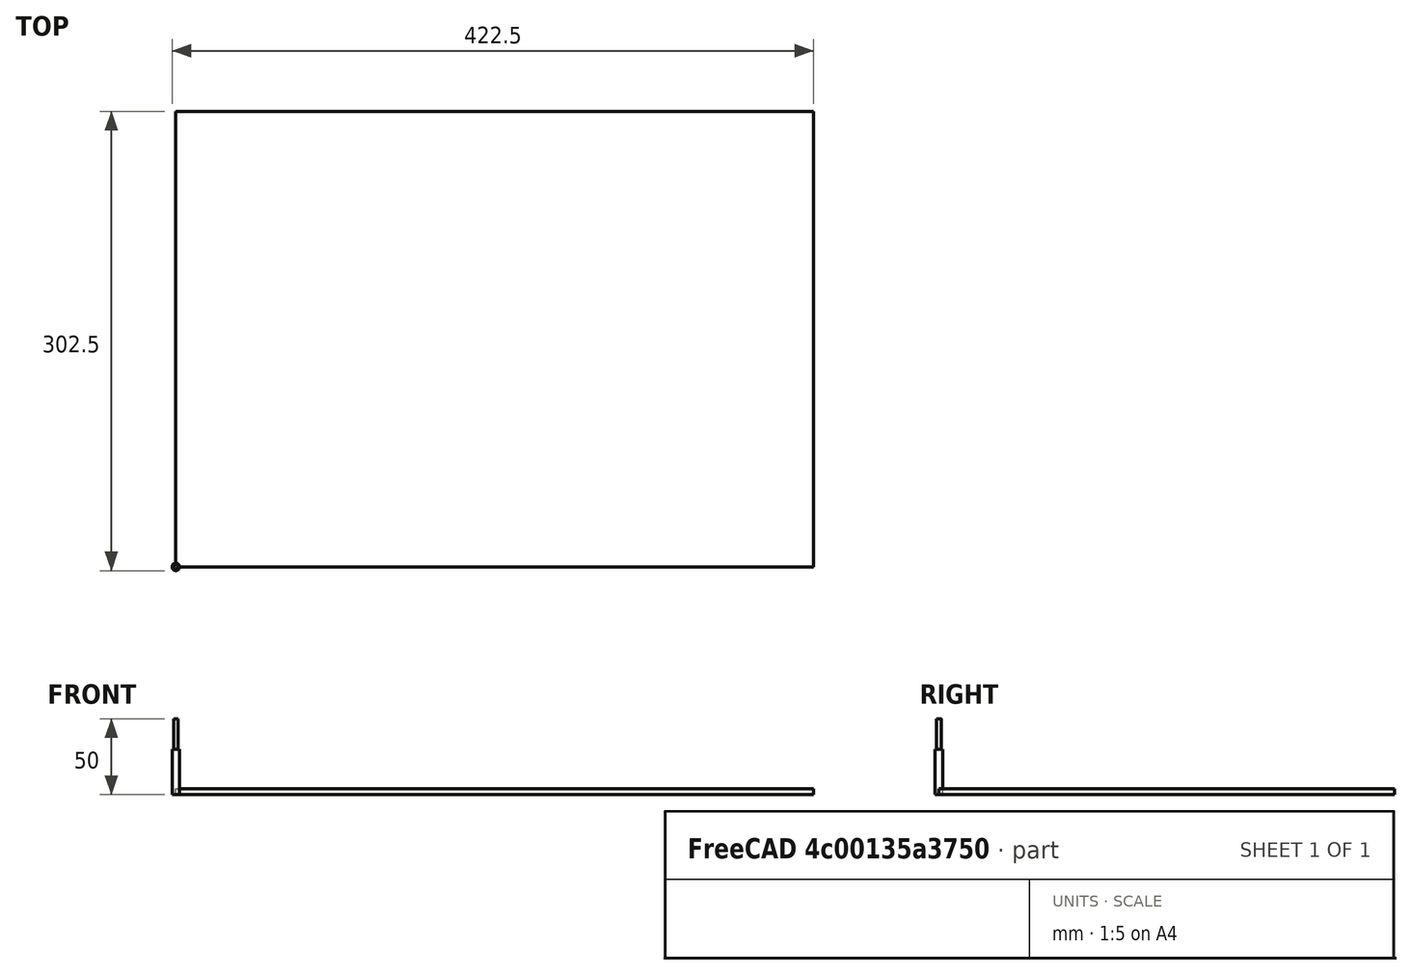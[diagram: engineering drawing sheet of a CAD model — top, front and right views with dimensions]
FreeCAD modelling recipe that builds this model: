
FCSTD DOCUMENT  (FreeCAD 1.0R39109 (Git))
Label: HousingAtari_LEVEL_2_T01
License: All rights reserved
LicenseURL: https://en.wikipedia.org/wiki/All_rights_reserved
objects: Sketcher::SketchObject×7, Part::Part2DObjectPython×5, TechDraw::DrawViewDraft×4, Path::FeaturePython×3, App::DocumentObjectGroup×3, Part::FeaturePython×2, PartDesign::Body×1, App::FeaturePython×1, Mesh::FeaturePython×1, TechDraw::DrawSVGTemplate×1, TechDraw::DrawPage×1
note: 22 computed .brp shape members not serialized (recipe doc carries the construction recipe); baked Part::Feature solids carry a one-line shape summary decoded from their .brp

FEATURE [Sketcher::SketchObject] Sketch  label="A3"
  ArcFitTolerance = 0
  FullyConstrained = true
  MakeInternals = false
  MapMode = 5
  sketch-geometry (6):
    g0: LineSegment StartX=0 StartY=0 StartZ=0 EndX=420 EndY=0 EndZ=0
    g1: LineSegment StartX=420 StartY=0 StartZ=0 EndX=420 EndY=297 EndZ=0
    g2: LineSegment StartX=0 StartY=297 StartZ=0 EndX=0 EndY=0 EndZ=0
    g3: LineSegment StartX=0 StartY=297 StartZ=0 EndX=210 EndY=297 EndZ=0
    g4: LineSegment StartX=210 StartY=297 StartZ=0 EndX=420 EndY=297 EndZ=0
    g5: LineSegment StartX=210 StartY=297 StartZ=0 EndX=210 EndY=0 EndZ=0
  constraints (16):
    c: Coincident(g0,g1)
    c: Coincident(g2,g0)
    c: Horizontal(g0)
    c: Vertical(g1)
    c: Vertical(g2)
    c: Coincident(g0,g-1)
    c: DistanceX(g2,g1) = 420
    c: DistanceY(g2,g2) = 297
    c: Coincident(g3,g2)
    c: Horizontal(g3)
    c: Coincident(g4,g3)
    c: Coincident(g4,g1)
    c: Horizontal(g4)
    c: Equal(g4,g3)
    c: Coincident(g5,g3)
    c: Symmetric(g0,g0,g5)
FEATURE [Sketcher::SketchObject] Sketch001  label="BOX-OUTLINE"
  ArcFitTolerance = 0
  FullyConstrained = true
  MakeInternals = false
  MapMode = 5
  sketch-geometry (59):
    g0: LineSegment StartX=45 StartY=255 StartZ=0 EndX=45 EndY=220 EndZ=0
    g1: LineSegment StartX=45 StartY=220 StartZ=0 EndX=45 EndY=185 EndZ=0
    g2: LineSegment StartX=45 StartY=185 StartZ=0 EndX=110 EndY=185 EndZ=0
    g3: LineSegment StartX=110 StartY=185 StartZ=0 EndX=175 EndY=185 EndZ=0
    g4: LineSegment StartX=175 StartY=185 StartZ=0 EndX=175 EndY=220 EndZ=0
    g5: LineSegment StartX=175 StartY=220 StartZ=0 EndX=175 EndY=255 EndZ=0
    g6: LineSegment StartX=175 StartY=255 StartZ=0 EndX=110 EndY=255 EndZ=0
    g7: LineSegment StartX=110 StartY=255 StartZ=0 EndX=45 EndY=255 EndZ=0
    g8: LineSegment StartX=45 StartY=185 StartZ=0 EndX=0 EndY=0 EndZ=0
    g9: LineSegment StartX=45 StartY=185 StartZ=0 EndX=45 EndY=181 EndZ=0
    g10: LineSegment StartX=45 StartY=181 StartZ=0 EndX=175 EndY=181 EndZ=0
    g11: LineSegment StartX=175 StartY=181 StartZ=0 EndX=175 EndY=185 EndZ=0
    g12: LineSegment StartX=175 StartY=185 StartZ=0 EndX=171 EndY=185 EndZ=0
    g13: LineSegment StartX=171 StartY=185 StartZ=0 EndX=171 EndY=255 EndZ=0
    g14: LineSegment StartX=171 StartY=255 StartZ=0 EndX=175 EndY=255 EndZ=0
    g15: LineSegment StartX=175 StartY=255 StartZ=0 EndX=175 EndY=259 EndZ=0
    g16: LineSegment StartX=175 StartY=259 StartZ=0 EndX=45 EndY=259 EndZ=0
    g17: LineSegment StartX=45 StartY=259 StartZ=0 EndX=45 EndY=255 EndZ=0
    g18: LineSegment StartX=45 StartY=185 StartZ=0 EndX=49 EndY=185 EndZ=0
    g19: LineSegment StartX=49 StartY=185 StartZ=0 EndX=49 EndY=255 EndZ=0
    g20: LineSegment StartX=49 StartY=255 StartZ=0 EndX=45 EndY=255 EndZ=0
    g21: LineSegment StartX=45 StartY=181 StartZ=0 EndX=45 EndY=151 EndZ=0
    g22: LineSegment StartX=45 StartY=151 StartZ=0 EndX=175 EndY=151 EndZ=0
    g23: LineSegment StartX=175 StartY=151 StartZ=0 EndX=175 EndY=181 EndZ=0
    g24: LineSegment StartX=171 StartY=185 StartZ=0 EndX=205 EndY=185 EndZ=0
    g25: LineSegment StartX=205 StartY=185 StartZ=0 EndX=205 EndY=255 EndZ=0
    g26: LineSegment StartX=205 StartY=255 StartZ=0 EndX=171 EndY=255 EndZ=0
    g27: LineSegment StartX=175 StartY=259 StartZ=0 EndX=175 EndY=289 EndZ=0
    g28: LineSegment StartX=175 StartY=289 StartZ=0 EndX=45 EndY=289 EndZ=0
    g29: LineSegment StartX=45 StartY=289 StartZ=0 EndX=45 EndY=259 EndZ=0
    g30: LineSegment StartX=49 StartY=255 StartZ=0 EndX=15 EndY=255 EndZ=0
    g31: LineSegment StartX=15 StartY=255 StartZ=0 EndX=15 EndY=185 EndZ=0
    g32: LineSegment StartX=15 StartY=185 StartZ=0 EndX=49 EndY=185 EndZ=0
    g33: LineSegment StartX=175 StartY=151 StartZ=0 EndX=171 EndY=151 EndZ=0
    g34: LineSegment StartX=171 StartY=151 StartZ=0 EndX=171 EndY=185 EndZ=0
    g35: LineSegment StartX=175 StartY=181 StartZ=0 EndX=205 EndY=181 EndZ=0
    g36: LineSegment StartX=205 StartY=181 StartZ=0 EndX=205 EndY=185 EndZ=0
    g37: LineSegment StartX=175 StartY=259 StartZ=0 EndX=205 EndY=259 EndZ=0
    g38: LineSegment StartX=205 StartY=259 StartZ=0 EndX=205 EndY=255 EndZ=0
    g39: LineSegment StartX=171 StartY=255 StartZ=0 EndX=171 EndY=289 EndZ=0
    g40: LineSegment StartX=171 StartY=289 StartZ=0 EndX=175 EndY=289 EndZ=0
    g41: LineSegment StartX=45 StartY=289 StartZ=0 EndX=49 EndY=289 EndZ=0
    g42: LineSegment StartX=49 StartY=289 StartZ=0 EndX=49 EndY=255 EndZ=0
    g43: LineSegment StartX=15 StartY=255 StartZ=0 EndX=15 EndY=259 EndZ=0
    g44: LineSegment StartX=15 StartY=259 StartZ=0 EndX=45 EndY=259 EndZ=0
    g45: LineSegment StartX=15 StartY=185 StartZ=0 EndX=15 EndY=181 EndZ=0
    g46: LineSegment StartX=15 StartY=181 StartZ=0 EndX=45 EndY=181 EndZ=0
    g47: LineSegment StartX=49 StartY=185 StartZ=0 EndX=49 EndY=151 EndZ=0
    g48: LineSegment StartX=49 StartY=151 StartZ=0 EndX=45 EndY=151 EndZ=0
    g49: LineSegment StartX=45 StartY=151 StartZ=0 EndX=45 EndY=77 EndZ=0
    g50: LineSegment StartX=45 StartY=77 StartZ=0 EndX=175 EndY=77 EndZ=0
    g51: LineSegment StartX=175 StartY=77 StartZ=0 EndX=175 EndY=151 EndZ=0
    g52: LineSegment StartX=49 StartY=151 StartZ=0 EndX=49 EndY=81 EndZ=0
    g53: LineSegment StartX=49 StartY=81 StartZ=0 EndX=171 EndY=81 EndZ=0
    g54: LineSegment StartX=171 StartY=81 StartZ=0 EndX=171 EndY=151 EndZ=0
    g55: LineSegment StartX=49 StartY=155 StartZ=0 EndX=171 EndY=155 EndZ=0
    g56: LineSegment StartX=49 StartY=81 StartZ=0 EndX=49 EndY=77 EndZ=0
    g57: LineSegment StartX=171 StartY=81 StartZ=0 EndX=171 EndY=77 EndZ=0
    g58: LineSegment StartX=49 StartY=285 StartZ=0 EndX=171 EndY=285 EndZ=0
  constraints (162):
    c: Vertical(g0)
    c: Coincident(g1,g0)
    c: Vertical(g1)
    c: Coincident(g2,g1)
    c: Horizontal(g2)
    c: Coincident(g3,g2)
    c: Horizontal(g3)
    c: Coincident(g4,g3)
    c: Vertical(g4)
    c: Coincident(g5,g4)
    c: Vertical(g5)
    c: Horizontal(g6)
    c: Coincident(g7,g6)
    c: Coincident(g7,g0)
    c: Horizontal(g7)
    c: Vertical(g2,g6)
    c: Horizontal(g0,g4)
    c: Equal(g4,g5)
    c: Equal(g7,g6)
    c: Coincident(g5,g6)
    c: DistanceY(g1,g0) = 70
    c: DistanceX(g0,g5) = 130
    c: Coincident(g8,g1)
    c: Coincident(g8,g-1)
    c: DistanceX(g8,g8) = 45
    c: DistanceY(g8,g8) = 185
    c: Coincident(g9,g1)
    c: Vertical(g9)
    c: Coincident(g10,g9)
    c: Horizontal(g10)
    c: Coincident(g11,g10)
    c: Coincident(g11,g3)
    c: Vertical(g11)
    c: Coincident(g12,g3)
    c: Horizontal(g12)
    c: Coincident(g13,g12)
    c: Vertical(g13)
    c: Coincident(g14,g13)
    c: Coincident(g14,g5)
    c: Horizontal(g14)
    c: Equal(g11,g12)
    c: DistanceY(g11,g11) = 4
    c: Coincident(g15,g5)
    c: Vertical(g15)
    c: Coincident(g16,g15)
    c: Horizontal(g16)
    c: Coincident(g17,g16)
    c: Coincident(g17,g0)
    c: Vertical(g17)
    c: Equal(g14,g15)
    c: Coincident(g18,g1)
    c: Horizontal(g18)
    c: Coincident(g19,g18)
    c: Vertical(g19)
    c: Coincident(g20,g19)
    c: Coincident(g20,g0)
    c: Horizontal(g20)
    c: Equal(g17,g20)
    c: Coincident(g21,g9)
    c: Vertical(g21)
    c: Coincident(g22,g21)
    c: Horizontal(g22)
    c: Coincident(g23,g22)
    c: Coincident(g23,g10)
    c: Coincident(g24,g12)
    c: Horizontal(g24)
    c: Coincident(g25,g24)
    c: Vertical(g25)
    c: Coincident(g26,g25)
    c: Coincident(g26,g13)
    c: Horizontal(g26)
    c: Coincident(g27,g15)
    c: Vertical(g27)
    c: Coincident(g28,g27)
    c: Horizontal(g28)
    c: Coincident(g29,g28)
    c: Coincident(g29,g16)
    c: Coincident(g30,g19)
    c: Horizontal(g30)
    c: Coincident(g31,g30)
    c: Vertical(g31)
    c: Coincident(g32,g31)
    c: Coincident(g32,g18)
    c: Horizontal(g32)
    c: Vertical(g23)
    c: Coincident(g33,g22)
    c: Horizontal(g33)
    c: Coincident(g34,g33)
    c: Coincident(g34,g12)
    c: Vertical(g34)
    c: Coincident(g35,g10)
    c: Horizontal(g35)
    c: Coincident(g36,g35)
    c: Coincident(g36,g24)
    c: Coincident(g37,g15)
    c: Horizontal(g37)
    c: Coincident(g38,g37)
    c: Coincident(g38,g25)
    c: Coincident(g39,g13)
    c: Vertical(g39)
    c: Coincident(g40,g39)
    c: Coincident(g40,g27)
    c: Horizontal(g40)
    c: Coincident(g41,g28)
    c: Horizontal(g41)
    c: Coincident(g42,g41)
    c: Coincident(g42,g19)
    c: Coincident(g43,g30)
    c: Vertical(g43)
    c: Coincident(g44,g43)
    c: Coincident(g44,g16)
    c: Coincident(g45,g31)
    c: Vertical(g45)
    c: Coincident(g46,g45)
    c: Coincident(g46,g9)
    c: Horizontal(g46)
    c: Coincident(g47,g18)
    c: Coincident(g48,g47)
    c: Coincident(g48,g21)
    c: Vertical(g38)
    c: Vertical(g47)
    c: Vertical(g36)
    c: Horizontal(g44)
    c: Horizontal(g48)
    c: DistanceY(g16,g28) = 30
    c: Vertical(g42)
    c: Vertical(g29)
    c: DistanceY(g23,g23) = 30
    c: Distance(g44,g44) = 30
    c: DistanceX(g35,g35) = 30
    c: Coincident(g49,g21)
    c: Vertical(g49)
    c: Coincident(g50,g49)
    c: Horizontal(g50)
    c: Coincident(g51,g50)
    c: Coincident(g51,g22)
    c: Vertical(g51)
    c: Coincident(g52,g47)
    c: Vertical(g52)
    c: Coincident(g53,g52)
    c: Horizontal(g53)
    c: Coincident(g54,g53)
    c: Coincident(g54,g33)
    c: Vertical(g54)
    c: PointOnObject(g55,g47)
    c: PointOnObject(g55,g34)
    c: Horizontal(g55)
    c: DistanceY(g47,g55) = 4
    c: Coincident(g56,g52)
    c: PointOnObject(g56,g50)
    c: Vertical(g56)
    c: DistanceY(g56,g56) = 4
    c: DistanceY(g52,g52) = 70
    c: DistanceY(g35,g37) = 78
    c: Coincident(g57,g53)
    c: PointOnObject(g57,g50)
    c: Vertical(g57)
    c: DistanceY(g57,g55) = 78
    c: PointOnObject(g58,g42)
    c: PointOnObject(g58,g39)
    c: Horizontal(g58)
    c: DistanceY(g58,g39) = 4
FEATURE [PartDesign::Body] Body
  AllowCompound = false
  Group = -> [Sketch,Sketch001]
  Origin = -> Origin
FEATURE [Sketcher::SketchObject] Sketch002  label="CUT-BOX-BASE"
  ArcFitTolerance = 0
  ExternalGeometry = -> [Sketch001]
  FullyConstrained = false
  MakeInternals = false
  MapMode = 5
  sketch-geometry (30):
    g0: LineSegment [constr] StartX=45 StartY=220 StartZ=0 EndX=175 EndY=220 EndZ=0
    g1: LineSegment [constr] StartX=110 StartY=185 StartZ=0 EndX=110 EndY=255 EndZ=0
    g2: LineSegment [constr] StartX=49 StartY=205 StartZ=0 EndX=171 EndY=205 EndZ=0
    g3: LineSegment [constr] StartX=49 StartY=235 StartZ=0 EndX=171 EndY=235 EndZ=0
    g4: LineSegment [constr] StartX=83.7703 StartY=185 StartZ=0 EndX=83.7703 EndY=255 EndZ=0
    g5: LineSegment [constr] StartX=133.77 StartY=185 StartZ=0 EndX=133.77 EndY=255 EndZ=0
    g6: LineSegment StartX=49 StartY=205 StartZ=0 EndX=49 EndY=220 EndZ=0
    g7: LineSegment StartX=49 StartY=220 StartZ=0 EndX=49 EndY=235 EndZ=0
    g8: LineSegment StartX=171 StartY=205 StartZ=0 EndX=171 EndY=220 EndZ=0
    g9: LineSegment StartX=171 StartY=220 StartZ=0 EndX=171 EndY=235 EndZ=0
    g10: LineSegment StartX=171 StartY=205 StartZ=0 EndX=175 EndY=205 EndZ=0
    g11: LineSegment StartX=171 StartY=235 StartZ=0 EndX=175 EndY=235 EndZ=0
    g12: LineSegment StartX=49 StartY=235 StartZ=0 EndX=45 EndY=235 EndZ=0
    g13: LineSegment StartX=49 StartY=205 StartZ=0 EndX=45 EndY=205 EndZ=0
    g14: LineSegment StartX=83.7703 StartY=185 StartZ=0 EndX=110 EndY=185 EndZ=0
    g15: LineSegment StartX=110 StartY=185 StartZ=0 EndX=133.77 EndY=185 EndZ=0
    g16: LineSegment StartX=83.7703 StartY=185 StartZ=0 EndX=83.7703 EndY=181 EndZ=0
    g17: LineSegment StartX=133.77 StartY=185 StartZ=0 EndX=133.77 EndY=181 EndZ=0
    g18: LineSegment StartX=83.7703 StartY=255 StartZ=0 EndX=110 EndY=255 EndZ=0
    g19: LineSegment StartX=110 StartY=255 StartZ=0 EndX=133.77 EndY=255 EndZ=0
    g20: LineSegment StartX=133.77 StartY=255 StartZ=0 EndX=133.77 EndY=259 EndZ=0
    g21: LineSegment StartX=83.7703 StartY=255 StartZ=0 EndX=83.7703 EndY=259 EndZ=0
    g22: LineSegment StartX=45 StartY=205 StartZ=0 EndX=45 EndY=181 EndZ=0
    g23: LineSegment StartX=45 StartY=181 StartZ=0 EndX=83.7703 EndY=181 EndZ=0
    g24: LineSegment StartX=133.77 StartY=181 StartZ=0 EndX=175 EndY=181 EndZ=0
    g25: LineSegment StartX=175 StartY=181 StartZ=0 EndX=175 EndY=205 EndZ=0
    g26: LineSegment StartX=175 StartY=235 StartZ=0 EndX=175 EndY=259 EndZ=0
    g27: LineSegment StartX=175 StartY=259 StartZ=0 EndX=133.77 EndY=259 EndZ=0
    g28: LineSegment StartX=83.7703 StartY=259 StartZ=0 EndX=45 EndY=259 EndZ=0
    g29: LineSegment StartX=45 StartY=259 StartZ=0 EndX=45 EndY=235 EndZ=0
  constraints (75):
    c: Coincident(g0,g-4)
    c: Coincident(g0,g-6)
    c: Coincident(g1,g-10)
    c: PointOnObject(g3,g-11)
    c: PointOnObject(g4,g-10)
    c: PointOnObject(g2,g-9)
    c: PointOnObject(g3,g-9)
    c: Horizontal(g2)
    c: Vertical(g4)
    c: Vertical(g5)
    c: Horizontal(g3)
    c: PointOnObject(g2,g-11)
    c: PointOnObject(g5,g-13)
    c: Coincident(g1,g-13)
    c: PointOnObject(g4,g-12)
    c: Coincident(g6,g2)
    c: Symmetric(g-11,g-11,g6)
    c: Coincident(g7,g6)
    c: Coincident(g7,g3)
    c: Equal(g6,g7)
    c: DistanceY(g2,g3) = 30
    c: DistanceX(g4,g5) = 50
    c: Coincident(g8,g2)
    c: Symmetric(g-9,g-9,g8)
    c: Coincident(g9,g8)
    c: Coincident(g9,g3)
    c: Coincident(g10,g2)
    c: PointOnObject(g10,g-6)
    c: Horizontal(g10)
    c: Coincident(g11,g3)
    c: PointOnObject(g11,g-5)
    c: Horizontal(g11)
    c: Coincident(g12,g3)
    c: PointOnObject(g12,g-4)
    c: Horizontal(g12)
    c: Coincident(g13,g2)
    c: PointOnObject(g13,g-3)
    c: Horizontal(g13)
    c: Coincident(g14,g4)
    c: Coincident(g14,g1)
    c: Coincident(g15,g1)
    c: Coincident(g15,g5)
    c: Horizontal(g15)
    c: Coincident(g16,g4)
    c: PointOnObject(g16,g-7)
    c: Vertical(g16)
    c: Coincident(g17,g5)
    c: PointOnObject(g17,g-7)
    c: Vertical(g17)
    c: Coincident(g18,g4)
    c: Coincident(g18,g1)
    c: Coincident(g19,g1)
    c: Coincident(g19,g5)
    c: Coincident(g20,g5)
    c: PointOnObject(g20,g-14)
    c: Vertical(g20)
    c: Coincident(g21,g4)
    c: PointOnObject(g21,g-14)
    c: Vertical(g21)
    c: Coincident(g22,g13)
    c: Coincident(g22,g-7)
    c: Coincident(g23,g22)
    c: Coincident(g23,g16)
    c: Coincident(g24,g17)
    c: Coincident(g24,g-7)
    c: Coincident(g25,g24)
    c: Coincident(g25,g10)
    c: Coincident(g26,g11)
    c: Coincident(g26,g-14)
    c: Coincident(g27,g26)
    c: Coincident(g27,g20)
    c: Coincident(g28,g21)
    c: Coincident(g28,g-14)
    c: Coincident(g29,g28)
    c: Coincident(g29,g12)
FEATURE [App::FeaturePython] SetupSheet  # Path/CAM operation (typed FeaturePython)
  ClearanceHeightExpression = OpStockZMax+SetupSheet.ClearanceHeightOffset
  ClearanceHeightOffset = 5
  CoolantMode = 0
  CoolantModes = None | Flood | Mist
  FinalDepthExpression = OpFinalDepth
  HorizRapid = 0
  SafeHeightExpression = OpStockZMax+SetupSheet.SafeHeightOffset
  SafeHeightOffset = 3
  StartDepthExpression = OpStartDepth
  StepDownExpression = OpToolDiameter
  VertRapid = 0
FEATURE [Part::Part2DObjectPython] Clone2D  label="Model-CUT-BOX"  # Draft 2D object (typed FeaturePython)
  Fuse = false
  Objects = -> [Sketch002]
  PathResource = Model
  Scale = (1,1,1)
FEATURE [Part::FeaturePython] ToolBit  label="Endmill"  # Path/CAM toolbit (typed FeaturePython)
  BitPropertyNames = Chipload | CuttingEdgeHeight | Diameter | Flutes | Length | Material | ShankDiameter | SpindleDirection
  BitShape = <path>
  Chipload = 0
  CuttingEdgeHeight = 30
  Diameter = 5
  Flutes = 0
  Length = 50
  Material = 0
  ShankDiameter = 3
  ShapeName = endmill
  SpindleDirection = 0
FEATURE [Path::FeaturePython] TC__Default_Tool  label="TC: Default Tool"  # Path/CAM operation (typed FeaturePython)
  HorizFeed = 1000
  HorizRapid = 1000
  SpindleDir = 0
  SpindleSpeed = 1000
  Tool = -> ToolBit
  ToolNumber = 1
  VertFeed = 1000
  VertRapid = 1000
  expr: HorizRapid = 1000
  expr: VertRapid = 1000
FEATURE [App::DocumentObjectGroup] Tools
  Group = -> [TC__Default_Tool]
FEATURE [Path::FeaturePython] Engrave  # Path/CAM operation (typed FeaturePython)
  Active = true
  ClearanceHeight = 9
  CoolantMode = 0
  CycleTime = 00:00:04
  FinalDepth = -5
  OpFinalDepth = -5
  OpStartDepth = 0
  OpStockZMax = 4
  OpStockZMin = 0
  OpToolDiameter = 5
  SafeHeight = 7
  StartDepth = 0
  StartVertex = 0
  StepDown = 5
  ToolController = -> TC__Default_Tool
  expr: ClearanceHeight = OpStockZMax + SetupSheet.ClearanceHeightOffset
  expr: FinalDepth = OpFinalDepth
  expr: SafeHeight = OpStockZMax + SetupSheet.SafeHeightOffset
  expr: StartDepth = OpStartDepth
  expr: StepDown = OpToolDiameter
FEATURE [App::DocumentObjectGroup] Operations
  Group = -> [Engrave]
FEATURE [Part::FeaturePython] Stock001  # WARN: FeaturePython — macro-defined, semantics opaque (R4)
  Height = 4
  Length = 420
  StockType = CreateBox
  Width = 300
FEATURE [Mesh::FeaturePython] CutMaterial  # WARN: FeaturePython — macro-defined, semantics opaque (R4)
FEATURE [Sketcher::SketchObject] Sketch004  label="CUT-BOX-WALLS"
  ArcFitTolerance = 0
  ExternalGeometry = -> [Sketch002,Sketch001]
  FullyConstrained = false
  MakeInternals = false
  MapMode = 5
  sketch-geometry (32):
    g0: LineSegment StartX=45 StartY=259 StartZ=0 EndX=30 EndY=259 EndZ=0
    g1: LineSegment StartX=30 StartY=259 StartZ=0 EndX=30 EndY=255 EndZ=0
    g2: LineSegment StartX=30 StartY=255 StartZ=0 EndX=15 EndY=255 EndZ=0
    g3: LineSegment StartX=15 StartY=185 StartZ=0 EndX=30 EndY=185 EndZ=0
    g4: LineSegment StartX=30 StartY=185 StartZ=0 EndX=30 EndY=181 EndZ=0
    g5: LineSegment StartX=30 StartY=181 StartZ=0 EndX=45 EndY=181 EndZ=0
    g6: LineSegment StartX=175 StartY=181 StartZ=0 EndX=190 EndY=181 EndZ=0
    g7: LineSegment StartX=190 StartY=181 StartZ=0 EndX=190 EndY=185 EndZ=0
    g8: LineSegment StartX=190 StartY=185 StartZ=0 EndX=205 EndY=185 EndZ=0
    g9: LineSegment StartX=205 StartY=255 StartZ=0 EndX=190 EndY=255 EndZ=0
    g10: LineSegment StartX=190 StartY=255 StartZ=0 EndX=190 EndY=259 EndZ=0
    g11: LineSegment StartX=190 StartY=259 StartZ=0 EndX=175 EndY=259 EndZ=0
    g12: LineSegment [constr] StartX=30 StartY=185 StartZ=0 EndX=30 EndY=255 EndZ=0
    g13: LineSegment [constr] StartX=190 StartY=185 StartZ=0 EndX=190 EndY=255 EndZ=0
    g14: LineSegment [constr] StartX=15 StartY=220 StartZ=0 EndX=205 EndY=220 EndZ=0
    g15: LineSegment [constr] StartX=110 StartY=151 StartZ=0 EndX=110 EndY=289 EndZ=0
    g16: LineSegment StartX=15 StartY=255 StartZ=0 EndX=15 EndY=235 EndZ=0
    g17: LineSegment StartX=15 StartY=235 StartZ=0 EndX=20.6579 EndY=235 EndZ=0
    g18: LineSegment StartX=20.6579 StartY=235 StartZ=0 EndX=20.6579 EndY=205 EndZ=0
    g19: LineSegment StartX=20.6579 StartY=204.687 StartZ=0 EndX=15 EndY=204.687 EndZ=0
    g20: LineSegment StartX=15 StartY=204.687 StartZ=0 EndX=15 EndY=185 EndZ=0
    g21: LineSegment StartX=205 StartY=185 StartZ=0 EndX=205 EndY=205 EndZ=0
    g22: LineSegment StartX=205 StartY=205 StartZ=0 EndX=199.009 EndY=205 EndZ=0
    g23: LineSegment StartX=199.009 StartY=205 StartZ=0 EndX=199.009 EndY=235 EndZ=0
    g24: LineSegment StartX=199.009 StartY=235 StartZ=0 EndX=205 EndY=235 EndZ=0
    g25: LineSegment StartX=205 StartY=235 StartZ=0 EndX=205 EndY=255 EndZ=0
    g26: LineSegment [constr] StartX=20.6579 StartY=235 StartZ=0 EndX=45 EndY=235 EndZ=0
    g27: LineSegment [constr] StartX=49 StartY=235 StartZ=0 EndX=170.368 EndY=235 EndZ=0
    g28: LineSegment [constr] StartX=175 StartY=235 StartZ=0 EndX=199.009 EndY=235 EndZ=0
    g29: LineSegment [constr] StartX=22.3684 StartY=205 StartZ=0 EndX=45 EndY=205 EndZ=0
    g30: LineSegment [constr] StartX=49.8267 StartY=205 StartZ=0 EndX=171 EndY=205 EndZ=0
    g31: LineSegment [constr] StartX=175 StartY=205 StartZ=0 EndX=199.009 EndY=205 EndZ=0
  constraints (82):
    c: Coincident(g0,g-18)
    c: Horizontal(g0)
    c: Coincident(g1,g0)
    c: Vertical(g1)
    c: Coincident(g2,g1)
    c: Coincident(g2,g-20)
    c: Horizontal(g2)
    c: Horizontal(g3)
    c: Coincident(g4,g3)
    c: Vertical(g4)
    c: Coincident(g5,g4)
    c: Coincident(g5,g-7)
    c: Horizontal(g5)
    c: Coincident(g6,g-11)
    c: Horizontal(g6)
    c: Coincident(g7,g6)
    c: Vertical(g7)
    c: Coincident(g8,g7)
    c: Coincident(g8,g-21)
    c: Horizontal(g8)
    c: Horizontal(g9)
    c: Coincident(g10,g9)
    c: Vertical(g10)
    c: Coincident(g11,g10)
    c: Coincident(g11,g-15)
    c: Horizontal(g11)
    c: Coincident(g12,g3)
    c: Coincident(g12,g1)
    c: Vertical(g12)
    c: Coincident(g13,g7)
    c: Coincident(g13,g9)
    c: Vertical(g13)
    c: Equal(g2,g0)
    c: Equal(g9,g11)
    c: DistanceX(g2,g2) = 15
    c: Distance(g9,g9) = 15
    c: PointOnObject(g14,g-20)
    c: PointOnObject(g14,g-21)
    c: Horizontal(g14)
    c: Symmetric(g-22,g-22,g15)
    c: Symmetric(g-19,g-19,g15)
    c: PointOnObject(g-13,g14)
    c: Coincident(g16,g2)
    c: PointOnObject(g16,g-20)
    c: Coincident(g17,g16)
    c: Horizontal(g17)
    c: Coincident(g18,g17)
    c: Vertical(g18)
    c: PointOnObject(g19,g-20)
    c: Horizontal(g19)
    c: Coincident(g20,g19)
    c: Coincident(g20,g3)
    c: Vertical(g20)
    c: Coincident(g21,g8)
    c: PointOnObject(g21,g-21)
    c: Coincident(g22,g21)
    c: Horizontal(g22)
    c: Coincident(g23,g22)
    c: Vertical(g23)
    c: Coincident(g24,g23)
    c: PointOnObject(g24,g-21)
    c: Horizontal(g24)
    c: PointOnObject(g25,g-21)
    c: Coincident(g25,g9)
    c: Vertical(g25)
    c: Horizontal(g17,g-3)
    c: Horizontal(g18,g-6)
    c: Horizontal(g-11,g22)
    c: Horizontal(g-14,g23)
    c: Coincident(g26,g17)
    c: Coincident(g26,g-3)
    c: Coincident(g27,g-4)
    c: Horizontal(g27)
    c: Coincident(g28,g-14)
    c: Coincident(g28,g23)
    c: Coincident(g29,g-6)
    c: Horizontal(g29)
    c: Coincident(g30,g-12)
    c: Horizontal(g30)
    c: Coincident(g31,g-11)
    c: Coincident(g31,g22)
    c: PointOnObject(g25,g24)
FEATURE [Sketcher::SketchObject] Sketch005  label="CUT-BOX-WALS2"
  ArcFitTolerance = 0
  ExternalGeometry = -> [Sketch002,Sketch001]
  FullyConstrained = true
  MakeInternals = false
  MapMode = 5
  sketch-geometry (28):
    g0: LineSegment [constr] StartX=83.7703 StartY=181 StartZ=0 EndX=83.7703 EndY=151 EndZ=0
    g1: LineSegment [constr] StartX=133.77 StartY=181 StartZ=0 EndX=133.77 EndY=151 EndZ=0
    g2: LineSegment StartX=83.7703 StartY=151 StartZ=0 EndX=83.7703 EndY=155 EndZ=0
    g3: LineSegment StartX=83.7703 StartY=155 StartZ=0 EndX=133.77 EndY=155 EndZ=0
    g4: LineSegment StartX=133.77 StartY=155 StartZ=0 EndX=133.77 EndY=151 EndZ=0
    g5: LineSegment [constr] StartX=83.7703 StartY=259 StartZ=0 EndX=83.7703 EndY=289 EndZ=0
    g6: LineSegment [constr] StartX=133.77 StartY=259 StartZ=0 EndX=133.77 EndY=289 EndZ=0
    g7: LineSegment [constr] StartX=49 StartY=166 StartZ=0 EndX=171 EndY=166 EndZ=0
    g8: LineSegment StartX=45 StartY=166 StartZ=0 EndX=49 EndY=166 EndZ=0
    g9: LineSegment StartX=175 StartY=166 StartZ=0 EndX=171 EndY=166 EndZ=0
    g10: LineSegment [constr] StartX=175 StartY=274 StartZ=0 EndX=45 EndY=274 EndZ=0
    g11: LineSegment StartX=45 StartY=274 StartZ=0 EndX=49 EndY=274 EndZ=0
    g12: LineSegment StartX=175 StartY=274 StartZ=0 EndX=171 EndY=274 EndZ=0
    g13: LineSegment StartX=83.7703 StartY=289 StartZ=0 EndX=83.7703 EndY=285 EndZ=0
    g14: LineSegment StartX=83.7703 StartY=285 StartZ=0 EndX=133.77 EndY=285 EndZ=0
    g15: LineSegment StartX=133.77 StartY=285 StartZ=0 EndX=133.77 EndY=289 EndZ=0
    g16: LineSegment StartX=49 StartY=181 StartZ=0 EndX=49 EndY=166 EndZ=0
    g17: LineSegment StartX=45 StartY=166 StartZ=0 EndX=45 EndY=151 EndZ=0
    g18: LineSegment StartX=45 StartY=151 StartZ=0 EndX=83.7703 EndY=151 EndZ=0
    g19: LineSegment StartX=133.77 StartY=151 StartZ=0 EndX=175 EndY=151 EndZ=0
    g20: LineSegment StartX=175 StartY=151 StartZ=0 EndX=175 EndY=166 EndZ=0
    g21: LineSegment StartX=171 StartY=166 StartZ=0 EndX=171 EndY=181 EndZ=0
    g22: LineSegment StartX=49 StartY=259 StartZ=0 EndX=49 EndY=274 EndZ=0
    g23: LineSegment StartX=45 StartY=274 StartZ=0 EndX=45 EndY=289 EndZ=0
    g24: LineSegment StartX=45 StartY=289 StartZ=0 EndX=83.7703 EndY=289 EndZ=0
    g25: LineSegment StartX=133.77 StartY=289 StartZ=0 EndX=175 EndY=289 EndZ=0
    g26: LineSegment StartX=175 StartY=289 StartZ=0 EndX=175 EndY=274 EndZ=0
    g27: LineSegment StartX=171 StartY=274 StartZ=0 EndX=171 EndY=259 EndZ=0
  constraints (75):
    c: PointOnObject(g7,g-11)
    c: Coincident(g0,g-4)
    c: PointOnObject(g0,g-9)
    c: Vertical(g0)
    c: Coincident(g1,g-3)
    c: PointOnObject(g1,g-9)
    c: Vertical(g1)
    c: Coincident(g2,g0)
    c: PointOnObject(g2,g-10)
    c: Vertical(g2)
    c: Coincident(g3,g2)
    c: PointOnObject(g3,g-10)
    c: Coincident(g4,g3)
    c: Coincident(g4,g1)
    c: Vertical(g4)
    c: Coincident(g5,g-5)
    c: PointOnObject(g5,g-17)
    c: Vertical(g5)
    c: Coincident(g6,g-6)
    c: Vertical(g6)
    c: Horizontal(g7)
    c: PointOnObject(g7,g-8)
    c: PointOnObject(g8,g-7)
    c: Coincident(g8,g7)
    c: Horizontal(g8)
    c: Coincident(g9,g7)
    c: Horizontal(g9)
    c: Symmetric(g-13,g-13,g10)
    c: Symmetric(g-16,g-16,g10)
    c: Coincident(g11,g10)
    c: PointOnObject(g11,g10)
    c: Coincident(g12,g10)
    c: PointOnObject(g12,g10)
    c: PointOnObject(g6,g-17)
    c: Coincident(g13,g5)
    c: PointOnObject(g13,g5)
    c: Coincident(g14,g13)
    c: PointOnObject(g14,g6)
    c: Horizontal(g14)
    c: Coincident(g15,g14)
    c: Coincident(g15,g6)
    c: PointOnObject(g14,g-24)
    c: DistanceY(g9,g-20) = 15
    c: DistanceY(g-18,g10) = 15
    c: PointOnObject(g16,g-20)
    c: Coincident(g16,g7)
    c: Vertical(g16)
    c: Coincident(g17,g8)
    c: Coincident(g17,g-9)
    c: Coincident(g18,g17)
    c: Coincident(g18,g0)
    c: Coincident(g19,g1)
    c: Coincident(g19,g-12)
    c: Coincident(g20,g19)
    c: Coincident(g20,g9)
    c: Vertical(g20)
    c: Coincident(g21,g7)
    c: PointOnObject(g21,g-20)
    c: Vertical(g21)
    c: PointOnObject(g22,g-18)
    c: Coincident(g22,g11)
    c: Vertical(g22)
    c: Coincident(g23,g10)
    c: Coincident(g23,g-17)
    c: Coincident(g24,g23)
    c: Coincident(g24,g5)
    c: Coincident(g25,g6)
    c: Coincident(g25,g-17)
    c: Coincident(g26,g25)
    c: Coincident(g26,g10)
    c: Coincident(g27,g12)
    c: PointOnObject(g27,g-18)
    c: Vertical(g27)
    c: PointOnObject(g11,g-15)
    c: PointOnObject(g12,g-14)
FEATURE [Sketcher::SketchObject] Sketch006  label="CUT-ROOF"
  ArcFitTolerance = 0
  ExternalGeometry = -> [Sketch005,Sketch004,Sketch001]
  FullyConstrained = false
  MakeInternals = false
  MapMode = 2
  sketch-geometry (22):
    g0: LineSegment [constr] StartX=218.305 StartY=259 StartZ=0 EndX=218.305 EndY=181 EndZ=0
    g1: LineSegment [constr] StartX=190 StartY=181 StartZ=0 EndX=218.305 EndY=181 EndZ=0
    g2: LineSegment [constr] StartX=190 StartY=259 StartZ=0 EndX=218.305 EndY=259 EndZ=0
    g3: LineSegment StartX=49 StartY=151 StartZ=0 EndX=49 EndY=131 EndZ=0
    g4: LineSegment [constr] StartX=83.7703 StartY=151 StartZ=0 EndX=83.7703 EndY=77 EndZ=0
    g5: LineSegment [constr] StartX=133.77 StartY=151 StartZ=0 EndX=133.77 EndY=77 EndZ=0
    g6: LineSegment [constr] StartX=49 StartY=131 StartZ=0 EndX=171 EndY=131 EndZ=0
    g7: LineSegment [constr] StartX=49 StartY=101 StartZ=0 EndX=171 EndY=101 EndZ=0
    g8: LineSegment StartX=49 StartY=131 StartZ=0 EndX=45 EndY=131 EndZ=0
    g9: LineSegment StartX=45 StartY=131 StartZ=0 EndX=45 EndY=101 EndZ=0
    g10: LineSegment StartX=45 StartY=101 StartZ=0 EndX=49 EndY=101 EndZ=0
    g11: LineSegment StartX=49 StartY=101 StartZ=0 EndX=49 EndY=81 EndZ=0
    g12: LineSegment StartX=49 StartY=81 StartZ=0 EndX=83.7703 EndY=81 EndZ=0
    g13: LineSegment StartX=83.7703 StartY=81 StartZ=0 EndX=83.7703 EndY=77 EndZ=0
    g14: LineSegment StartX=83.7703 StartY=77 StartZ=0 EndX=133.77 EndY=77 EndZ=0
    g15: LineSegment StartX=133.77 StartY=77 StartZ=0 EndX=133.77 EndY=81 EndZ=0
    g16: LineSegment StartX=133.77 StartY=81 StartZ=0 EndX=171 EndY=81 EndZ=0
    g17: LineSegment StartX=171 StartY=81 StartZ=0 EndX=171 EndY=101 EndZ=0
    g18: LineSegment StartX=171 StartY=101 StartZ=0 EndX=175 EndY=101 EndZ=0
    g19: LineSegment StartX=175 StartY=101 StartZ=0 EndX=175 EndY=131 EndZ=0
    g20: LineSegment StartX=175 StartY=131 StartZ=0 EndX=171 EndY=131 EndZ=0
    g21: LineSegment StartX=171 StartY=131 StartZ=0 EndX=171 EndY=151 EndZ=0
  constraints (61):
    c: Vertical(g0)
    c: Coincident(g1,g-9)
    c: Coincident(g1,g0)
    c: Coincident(g2,g-8)
    c: Coincident(g2,g0)
    c: Horizontal(g2)
    c: Horizontal(g1)
    c: DistanceY(g0,g0) = 78
    c: Coincident(g3,g-10)
    c: PointOnObject(g3,g-10)
    c: Coincident(g4,g-3)
    c: PointOnObject(g4,g-12)
    c: Vertical(g4)
    c: Coincident(g5,g-5)
    c: PointOnObject(g5,g-12)
    c: Vertical(g5)
    c: Coincident(g6,g3)
    c: PointOnObject(g6,g-14)
    c: Horizontal(g6)
    c: PointOnObject(g7,g-10)
    c: PointOnObject(g7,g-14)
    c: Horizontal(g7)
    c: Coincident(g8,g3)
    c: PointOnObject(g8,g-11)
    c: Coincident(g9,g8)
    c: PointOnObject(g9,g-11)
    c: Coincident(g10,g9)
    c: Coincident(g10,g7)
    c: Coincident(g11,g7)
    c: Coincident(g11,g-13)
    c: Coincident(g12,g11)
    c: PointOnObject(g12,g4)
    c: Horizontal(g12)
    c: Coincident(g13,g12)
    c: Coincident(g13,g4)
    c: Coincident(g14,g4)
    c: Coincident(g14,g5)
    c: Coincident(g15,g5)
    c: PointOnObject(g15,g-13)
    c: Vertical(g15)
    c: Coincident(g16,g15)
    c: Coincident(g16,g-14)
    c: Coincident(g17,g16)
    c: Coincident(g17,g7)
    c: Coincident(g18,g7)
    c: PointOnObject(g18,g-15)
    c: Horizontal(g18)
    c: Coincident(g19,g18)
    c: PointOnObject(g19,g-15)
    c: Coincident(g20,g19)
    c: Coincident(g20,g6)
    c: Coincident(g21,g6)
    c: Coincident(g21,g-14)
    c: Horizontal(g20)
    c: Horizontal(g8)
    c: DistanceY(g21,g21) = 20
    c: DistanceY(g17,g17) = 20
    c: Horizontal(g10)
    c: DistanceY(g-17,g-17) = 30
    c: Distance(g19,g19) = 30
    c: DistanceY(g11,g3) = 70
FEATURE [Part::Part2DObjectPython] Clone2D002  label="Model-CUT-BOX-WALLS"  # Draft 2D object (typed FeaturePython)
  Fuse = false
  Objects = -> [Sketch004]
  PathResource = Model
  Scale = (1,1,1)
FEATURE [Part::Part2DObjectPython] Clone2D003  label="Model-CUT-BOX-WALS2"  # Draft 2D object (typed FeaturePython)
  Fuse = false
  Objects = -> [Sketch005]
  PathResource = Model
  Scale = (1,1,1)
FEATURE [Sketcher::SketchObject] Sketch003  label="CUT-Functional"
  ArcFitTolerance = 0
  ExternalGeometry = -> [Sketch006,Sketch002,Clone2D003]
  FullyConstrained = false
  MakeInternals = false
  MapMode = 5
  sketch-geometry (38):
    g0: LineSegment [constr] StartX=49 StartY=151 StartZ=0 EndX=110 EndY=151 EndZ=0
    g1: LineSegment [constr] StartX=110 StartY=151 StartZ=0 EndX=171 EndY=151 EndZ=0
    g2: LineSegment [constr] StartX=171 StartY=131 StartZ=0 EndX=171 EndY=116 EndZ=0
    g3: LineSegment [constr] StartX=171 StartY=116 StartZ=0 EndX=171 EndY=101 EndZ=0
    g4: LineSegment StartX=110 StartY=141.519 StartZ=0 EndX=63.9482 EndY=141.519 EndZ=0
    g5: LineSegment StartX=110 StartY=141.519 StartZ=0 EndX=154.396 EndY=141.519 EndZ=0
    g6: LineSegment StartX=159.951 StartY=135.965 StartZ=0 EndX=159.951 EndY=116 EndZ=0
    g7: LineSegment StartX=159.951 StartY=116 StartZ=0 EndX=159.951 EndY=96.3153 EndZ=0
    g8: LineSegment StartX=154.396 StartY=90.7606 StartZ=0 EndX=63.7857 EndY=90.7606 EndZ=0
    g9: LineSegment StartX=59.5711 StartY=94.9753 StartZ=0 EndX=59.5711 EndY=137.142 EndZ=0
    g10: ArcOfCircle CenterX=63.9482 CenterY=137.142 CenterZ=0 NormalX=0 NormalY=0 NormalZ=1 AngleXU=0 Radius=4.3771 StartAngle=1.5708 EndAngle=3.14159
    g11: GeomPoint [constr] X=59.5711 Y=141.519 Z=0
    g12: ArcOfCircle CenterX=63.7857 CenterY=94.9753 CenterZ=0 NormalX=0 NormalY=0 NormalZ=1 AngleXU=0 Radius=4.21464 StartAngle=3.14159 EndAngle=4.71239
    g13: GeomPoint [constr] X=59.5711 Y=90.7606 Z=0
    g14: ArcOfCircle CenterX=154.396 CenterY=96.3153 CenterZ=0 NormalX=0 NormalY=0 NormalZ=1 AngleXU=0 Radius=5.55461 StartAngle=4.71239 EndAngle=6.28319
    g15: GeomPoint [constr] X=159.951 Y=90.7606 Z=0
    g16: ArcOfCircle CenterX=154.396 CenterY=135.965 CenterZ=0 NormalX=0 NormalY=0 NormalZ=1 AngleXU=0 Radius=5.55461 StartAngle=-9e-16 EndAngle=1.5708
    g17: GeomPoint [constr] X=159.951 Y=141.519 Z=0
    g18: LineSegment [constr] StartX=80 StartY=238.652 StartZ=0 EndX=110 EndY=238.652 EndZ=0
    g19: LineSegment [constr] StartX=110 StartY=238.652 StartZ=0 EndX=140 EndY=238.652 EndZ=0
    g20: Circle CenterX=80 CenterY=238.652 CenterZ=0 NormalX=0 NormalY=0 NormalZ=1 AngleXU=0 Radius=8
    g21: Circle CenterX=110 CenterY=238.652 CenterZ=0 NormalX=0 NormalY=0 NormalZ=1 AngleXU=0 Radius=8
    g22: Circle CenterX=140 CenterY=238.652 CenterZ=0 NormalX=0 NormalY=0 NormalZ=1 AngleXU=0 Radius=8
    g23: Circle CenterX=100 CenterY=193.322 CenterZ=0 NormalX=0 NormalY=0 NormalZ=1 AngleXU=0 Radius=1.5
    g24: Circle CenterX=110 CenterY=193.322 CenterZ=0 NormalX=0 NormalY=0 NormalZ=1 AngleXU=0 Radius=1.5
    g25: Circle CenterX=120 CenterY=193.322 CenterZ=0 NormalX=0 NormalY=0 NormalZ=1 AngleXU=0 Radius=1.5
    g26: LineSegment [constr] StartX=100 StartY=193.322 StartZ=0 EndX=110 EndY=193.322 EndZ=0
    g27: LineSegment [constr] StartX=110 StartY=193.322 StartZ=0 EndX=120 EndY=193.322 EndZ=0
    g28: Circle CenterX=33.9008 CenterY=220.697 CenterZ=0 NormalX=0 NormalY=0 NormalZ=1 AngleXU=0 Radius=8
    g29: Circle CenterX=95 CenterY=216.895 CenterZ=0 NormalX=0 NormalY=0 NormalZ=1 AngleXU=0 Radius=8
    g30: Circle CenterX=125 CenterY=216.895 CenterZ=0 NormalX=0 NormalY=0 NormalZ=1 AngleXU=0 Radius=8
    g31: LineSegment [constr] StartX=95 StartY=216.895 StartZ=0 EndX=110 EndY=216.895 EndZ=0
    g32: LineSegment [constr] StartX=110 StartY=216.895 StartZ=0 EndX=125 EndY=216.895 EndZ=0
    g33: LineSegment StartX=49 StartY=77 StartZ=0 EndX=49 EndY=7 EndZ=0
    g34: LineSegment StartX=49 StartY=7 StartZ=0 EndX=171 EndY=7 EndZ=0
    g35: LineSegment StartX=171 StartY=7 StartZ=0 EndX=171 EndY=77 EndZ=0
    g36: LineSegment StartX=49 StartY=77 StartZ=0 EndX=83.7703 EndY=77 EndZ=0
    g37: LineSegment StartX=171 StartY=77 StartZ=0 EndX=133.77 EndY=77 EndZ=0
  constraints (75):
    c: Coincident(g4,g5)
    c: Coincident(g6,g7)
    c: PointOnObject(g11,g9)
    c: PointOnObject(g11,g4)
    c: Tangent(g9,g10) = 1.5708
    c: Tangent(g4,g10) = -1.5708
    c: PointOnObject(g13,g9)
    c: PointOnObject(g13,g8)
    c: Tangent(g9,g12) = 1.5708
    c: Tangent(g8,g12) = 1.5708
    c: PointOnObject(g15,g8)
    c: PointOnObject(g15,g7)
    c: Tangent(g8,g14) = 1.5708
    c: Tangent(g7,g14) = 1.5708
    c: PointOnObject(g17,g6)
    c: PointOnObject(g17,g5)
    c: Tangent(g6,g16) = 1.5708
    c: Tangent(g5,g16) = 1.5708
    c: Vertical(g14,g16)
    c: Vertical(g6)
    c: Vertical(g7)
    c: Horizontal(g5)
    c: Horizontal(g4)
    c: Vertical(g9)
    c: Horizontal(g8)
    c: Horizontal(g18)
    c: Coincident(g19,g18)
    c: Horizontal(g19)
    c: Equal(g19,g18)
    c: Vertical(g18,g-6)
    c: Coincident(g20,g18)
    c: Coincident(g21,g18)
    c: Coincident(g22,g19)
    c: Equal(g22,g21)
    c: Equal(g21,g20)
    c: Diameter(g22) = 16
    c: DistanceX(g19,g19) = 30
    c: Equal(g25,g24)
    c: Equal(g24,g23)
    c: Diameter(g25) = 3
    c: Coincident(g26,g23)
    c: Coincident(g26,g24)
    c: Horizontal(g26)
    c: Coincident(g27,g24)
    c: Coincident(g27,g25)
    c: Horizontal(g27)
    c: Equal(g26,g27)
    c: DistanceX(g27,g27) = 10
    c: Vertical(g24,g21)
    c: Diameter(g28) = 16
    c: Equal(g30,g29)
    c: Equal(g30,g22)
    c: Coincident(g31,g29)
    c: Horizontal(g31)
    c: Coincident(g32,g31)
    c: Coincident(g32,g30)
    c: Horizontal(g32)
    c: Vertical(g31,g18)
    c: Equal(g31,g32)
    c: DistanceX(g29,g30) = 30
    c: Coincident(g33,g34)
    c: Coincident(g34,g35)
    c: Vertical(g33)
    c: Vertical(g35)
    c: Horizontal(g34)
    c: Vertical(g33,g-3)
    c: Vertical(g-5,g35)
    c: DistanceY(g35,g35) = 70
    c: DistanceY(g-5,g1) = 70
    c: Coincident(g36,g33)
    c: Coincident(g36,g-10)
    c: Coincident(g37,g35)
    c: Coincident(g37,g-10)
    c: Horizontal(g37)
    c: Horizontal(g36)
FEATURE [Part::Part2DObjectPython] Clone2D001  label="Model-CUT-Functional"  # Draft 2D object (typed FeaturePython)
  Fuse = false
  Objects = -> [Sketch003]
  PathResource = Model
  Scale = (1,1,1)
FEATURE [Part::Part2DObjectPython] Clone2D004  label="Model-CUT-ROOF"  # Draft 2D object (typed FeaturePython)
  Fuse = false
  Objects = -> [Sketch006]
  PathResource = Model
  Scale = (1,1,1)
FEATURE [App::DocumentObjectGroup] Model
  Group = -> [Clone2D,Clone2D001,Clone2D002,Clone2D003,Clone2D004]
FEATURE [Path::FeaturePython] Job  # Path/CAM operation (typed FeaturePython)
  CycleTime = 00:00:04
  Fixtures = G54
  GeometryTolerance = 0.01
  Group = -> [Sketch005]
  JobType = 0
  Model = -> Model
  Operations = -> Operations
  OrderOutputBy = 0
  PostProcessor = 10
  PostProcessorOutputFile = <userpath>/Documents/AdruinoAtariPaddle/FREECAD/HousingAtari_RAW.nc
  SetupSheet = -> SetupSheet
  SplitOutput = false
  Stock = -> Stock001
  Tools = -> Tools
FEATURE [TechDraw::DrawSVGTemplate] Template
  Height = 210
  Orientation = 1
  Template = <path>
  Width = 297
FEATURE [TechDraw::DrawViewDraft] DraftView001
  Direction = (0,0,1)
  FontSize = 12
  LineSpacing = 1
  LineStyle = Solid
  LineWidth = 0.35
  LockPosition = false
  OverrideStyle = false
  Rotation = 0
  Scale = 0.6
  ScaleType = 2
  Source = -> Sketch006
  Symbol = <svg\n	xmlns="http://www.w3.org/2000/svg" version="1.1"\n	xmlns:freecad="https://www.freecad.org/wiki/index.php?title=Svg_Namespace">\n<g transform ="scale(1,-1)">\n    <path id="Sketch006_w0000"  d="M 49.0 151.0 L 49.0 131.0 L 45.0 131.0 L 45.0 101.0 L 49.0 101.0 L 49.0 81.0 L 83.7703438155425 81.0 L 83.7703438155425 77.0 L 133.7703438155425 77.00000000000001 L 133.7703438155425 81.00000000000001 L 171.0 81.00000000000001 L 171.0 101.00000000000001 L 175.0 101.00000000000001 L 175.0 131.0 L 171.0 131.0 L 171.0 151.0 " stroke="#000000" stroke-width="1.1666666666666667 px" style="stroke-width:1.1666666666666667;stroke-miterlimit:4;stroke-dasharray:none;stroke-linecap:square;fill:none;fill-opacity:1;fill-rule: evenodd"/>\n</g>\n\n</svg>
  X = 147.769
  Y = 49.2811
FEATURE [TechDraw::DrawViewDraft] DraftView002
  Direction = (0,0,1)
  FontSize = 12
  LineSpacing = 1
  LineStyle = Solid
  LineWidth = 0.35
  LockPosition = false
  OverrideStyle = false
  Rotation = 0
  Scale = 0.6
  ScaleType = 2
  Source = -> Sketch005
  Symbol = <svg\n	xmlns="http://www.w3.org/2000/svg" version="1.1"\n	xmlns:freecad="https://www.freecad.org/wiki/index.php?title=Svg_Namespace">\n<g transform ="scale(1,-1)">\n    <path id="Sketch005_w0000"  d="M 48.99999999999998 181.0 L 48.99999999999998 166.0 L 45.0 166.0 L 45.0 151.0 L 83.7703438155425 151.0 L 83.7703438155425 155.0 L 133.7703438155425 155.0 L 133.7703438155425 151.0 L 175.0 151.0 L 175.0 166.0 L 171.0 166.0 L 171.0 181.0 " stroke="#000000" stroke-width="1.1666666666666667 px" style="stroke-width:1.1666666666666667;stroke-miterlimit:4;stroke-dasharray:none;stroke-linecap:square;fill:none;fill-opacity:1;fill-rule: evenodd"/>\n<path id="Sketch005_w0001"  d="M 48.99999999999997 259.0 L 48.99999999999997 274.0 L 45.0 274.0 L 45.0 289.0 L 83.7703438155425 289.0 L 83.7703438155425 285.0 L 133.77034381554242 285.0 L 133.7703438155425 289.0 L 175.0 289.0 L 175.0 274.0 L 171.0 274.0 L 171.0 259.0 " stroke="#000000" stroke-width="1.1666666666666667 px" style="stroke-width:1.1666666666666667;stroke-miterlimit:4;stroke-dasharray:none;stroke-linecap:square;fill:none;fill-opacity:1;fill-rule: evenodd"/>\n</g>\n\n</svg>
  X = 147.769
  Y = 113.527
FEATURE [TechDraw::DrawViewDraft] DraftView003
  Direction = (0,0,1)
  FontSize = 12
  LineSpacing = 1
  LineStyle = Solid
  LineWidth = 0.35
  LockPosition = false
  OverrideStyle = false
  Rotation = 0
  Scale = 0.6
  ScaleType = 2
  Source = -> Sketch004
  Symbol = <svg\n	xmlns="http://www.w3.org/2000/svg" version="1.1"\n	xmlns:freecad="https://www.freecad.org/wiki/index.php?title=Svg_Namespace">\n<g transform ="scale(1,-1)">\n    <path id="Sketch004_w0000"  d="M 45.0 259.0 L 30.0 259.0 L 30.0 255.0 L 14.999999999999998 255.0 L 15.0 235.0 L 20.657879 235.0 L 20.657879 205.0 " stroke="#000000" stroke-width="1.1666666666666667 px" style="stroke-width:1.1666666666666667;stroke-miterlimit:4;stroke-dasharray:none;stroke-linecap:square;fill:none;fill-opacity:1;fill-rule: evenodd"/>\n<path id="Sketch004_w0001"  d="M 20.657879 204.687439 L 15.0 204.687439 L 15.0 185.0 L 30.0 185.0 L 30.0 181.0 L 45.0 181.0 " stroke="#000000" stroke-width="1.1666666666666667 px" style="stroke-width:1.1666666666666667;stroke-miterlimit:4;stroke-dasharray:none;stroke-linecap:square;fill:none;fill-opacity:1;fill-rule: evenodd"/>\n<path id="Sketch004_w0002"  d="M 175.0 181.0 L 190.0 181.0 L 190.0 185.0 L 205.0 185.0 L 205.0 205.0 L 199.0094149999999 205.0 L 199.0094149999999 235.0 L 205.0 234.99999999999974 L 205.0 255.0 L 190.0 255.0 L 190.0 259.0 L 175.0 259.0 " stroke="#000000" stroke-width="1.1666666666666667 px" style="stroke-width:1.1666666666666667;stroke-miterlimit:4;stroke-dasharray:none;stroke-linecap:square;fill:none;fill-opacity:1;fill-rule: evenodd"/>\n</g>\n\n</svg>
  X = 147.769
  Y = 114.014
FEATURE [TechDraw::DrawViewDraft] DraftView004
  Direction = (0,0,1)
  FontSize = 12
  LineSpacing = 1
  LineStyle = Solid
  LineWidth = 0.35
  LockPosition = false
  OverrideStyle = false
  Rotation = 0
  Scale = 0.6
  ScaleType = 2
  Source = -> Sketch002
  Symbol = <svg\n	xmlns="http://www.w3.org/2000/svg" version="1.1"\n	xmlns:freecad="https://www.freecad.org/wiki/index.php?title=Svg_Namespace">\n<g transform ="scale(1,-1)">\n    <path id="Sketch002_w0000"  d="M 45.0 181.0 L 83.7703438155425 181.0 L 83.7703438155425 185.00000000000003 L 110.0 185.0 L 133.7703438155425 185.0 L 133.7703438155425 181.0 L 175.0 181.0 L 175.0 205.0 L 171.0 205.0 L 171.0 220.0 L 171.0 235.0 L 175.0 235.0 L 175.0 259.0 L 133.7703438155425 259.0 L 133.7703438155425 255.0 L 110.0 255.0 L 83.7703438155425 255.0 L 83.7703438155425 259.0 L 45.0 259.0 L 45.0 235.0 L 49.0 235.0 L 49.0 220.0 L 49.0 205.0 L 45.0 205.0 L 45.0 181.0 " stroke="#000000" stroke-width="1.1666666666666667 px" style="stroke-width:1.1666666666666667;stroke-miterlimit:4;stroke-dasharray:none;stroke-linecap:square;fill:none;fill-opacity:1;fill-rule: evenodd"/>\n</g>\n\n</svg>
  X = 147.769
  Y = 114.014
FEATURE [TechDraw::DrawPage] Page
  KeepUpdated = true
  NextBalloonIndex = 1
  ProjectionType = 0
  Scale = 0.6
  Template = -> Template
  Views = -> [DraftView001,DraftView002,DraftView003,DraftView004]
note: 2 file-system paths scrubbed to <path> (originals preserved in the JSON sidecar)
